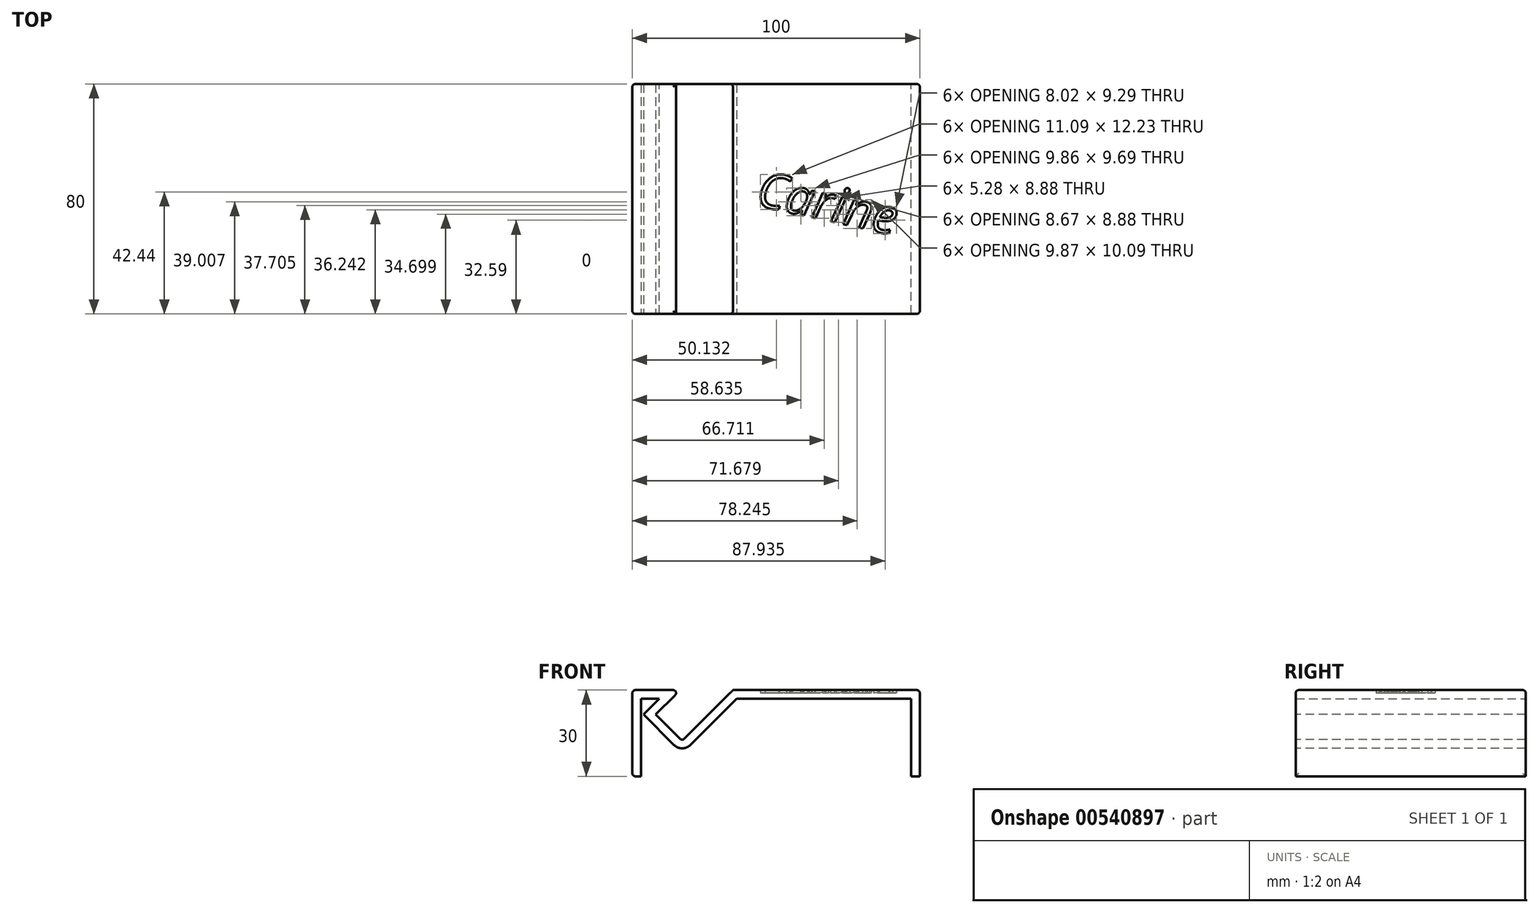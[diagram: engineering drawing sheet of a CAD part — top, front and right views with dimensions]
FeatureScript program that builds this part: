
annotation { "Feature Type Name" : "Feature", "Feature Type Description" : "" }
export const myFeature = defineFeature(function(context is Context, id is Id, definition is map)
    precondition{}
    {
        {
            var Q0;
            Q0=qCreatedBy(makeId("Top.planeOp"),FACE);
            var sketch = newSketch(context, id + "F0", { "sketchPlane" : qUnion([Q0])});
            skLineSegment(sketch, "E0.bottom", {"start": v(-50, -40) * mm, "end": v(50, -40) * mm});
            skLineSegment(sketch, "E0.top", {"start": v(-50, 40) * mm, "end": v(50, 40) * mm});
            skLineSegment(sketch, "E0.left", {"start": v(-50, -40) * mm, "end": v(-50, 40) * mm});
            skLineSegment(sketch, "E0.right", {"start": v(50, -40) * mm, "end": v(50, 40) * mm});
            skPoint(sketch, "E0.middle", {"position": v(0, 0) * mm});
            skSolve(sketch);
        }
        {
            var Q0;
            Q0=makeQuery(id+"F0.imprint","IMPRINT",FACE,{"disambiguationData":[TD([[makeQuery(id+"F0.imprint","IMPRINT",EDGE,{"derivedFrom":sQuery(id+"F0.wireOp",EDGE,"E0.bottom")}),1.0]])]});
            extrude(context, id + "F1", {"entities" : qUnion([Q0]), "depth" : 30 * mm, "offsetDistance" : 25 * mm});
        }
        {
            var Q0;
            Q0=makeQuery(id+"F1.opExtrude","SWEPT_FACE",FACE,{"disambiguationData":[OSD([sQuery(id+"F0.wireOp",EDGE,"E0.bottom")])]});
            var sketch = newSketch(context, id + "F2", { "sketchPlane" : qUnion([Q0])});
            skLineSegment(sketch, "E1.bottom", {"start": v(-32.68, 12.32) * mm, "end": v(-15, 30) * mm});
            skLineSegment(sketch, "E1.top", {"start": v(-41.87, 21.51) * mm, "end": v(-24.2, 39.2) * mm});
            skLineSegment(sketch, "E1.left", {"start": v(-32.68, 12.32) * mm, "end": v(-41.87, 21.51) * mm});
            skLineSegment(sketch, "E1.right", {"start": v(-15, 30) * mm, "end": v(-24.2, 39.2) * mm});
            skSolve(sketch);
        }
        {
            var Q0;
            Q0 = qSketchRegion(id + "F2", true);
            extrude(context, id + "F3", {"entities" : qUnion([Q0]), "operationType" : NewBodyOperationType.REMOVE, "oppositeDirection" : true, "depth" : 80 * mm, "offsetDistance" : 25 * mm});
        }
        {
            var Q0;
            Q0=makeQuery(id+"F3.boolean.opBoolean","INTERSECT",EDGE,{"derivedFrom":[makeQuery(id+"F1.opExtrude","CAP_FACE",FACE,{"disambiguationData":[OSD([sQuery(id+"F0.wireOp",EDGE,"E0.bottom"),sQuery(id+"F0.wireOp",EDGE,"E0.top"),sQuery(id+"F0.wireOp",EDGE,"E0.left"),sQuery(id+"F0.wireOp",EDGE,"E0.right")])],"isStart":false}),makeQuery(id+"F3.opExtrude","SWEPT_FACE",FACE,{"disambiguationData":[OSD([sQuery(id+"F2.wireOp",EDGE,"E1.top")])]})]});
            var Q1;
            Q1=makeQuery(id+"F3.boolean.opBoolean","COPY",EDGE,{"derivedFrom":makeQuery(id+"F3.opExtrude","SWEPT_EDGE",EDGE,{"disambiguationData":[OSD([sQuery(id+"F0.wireOp",EDGE,"E0.bottom"),sQuery(id+"F2.wireOp",EDGE,"E1.bottom"),sQuery(id+"F2.wireOp",EDGE,"E1.right")])]})});
            var Q2;
            Q2=makeQuery(id+"F3.boolean.opBoolean","COPY",EDGE,{"derivedFrom":makeQuery(id+"F3.opExtrude","CAP_EDGE",EDGE,{"disambiguationData":[OSD([sQuery(id+"F2.wireOp",EDGE,"E1.left")])],"isStart":true})});
            var Q3;
            Q3=makeQuery(id+"F3.boolean.opBoolean","COPY",EDGE,{"derivedFrom":makeQuery(id+"F3.opExtrude","SWEPT_EDGE",EDGE,{"disambiguationData":[OSD([sQuery(id+"F2.wireOp",EDGE,"E1.bottom"),sQuery(id+"F2.wireOp",EDGE,"E1.left")])]})});
            var Q4;
            Q4=makeQuery(id+"F1.opExtrude","CAP_EDGE",EDGE,{"disambiguationData":[OSD([sQuery(id+"F0.wireOp",EDGE,"E0.left")])],"isStart":false});
            var Q5;
            Q5=makeQuery(id+"F1.opExtrude","SWEPT_EDGE",EDGE,{"disambiguationData":[OSD([sQuery(id+"F0.wireOp",EDGE,"E0.top"),sQuery(id+"F0.wireOp",EDGE,"E0.left")])]});
            var Q6;
            Q6=makeQuery(id+"F1.opExtrude","CAP_EDGE",EDGE,{"disambiguationData":[OSD([sQuery(id+"F0.wireOp",EDGE,"E0.left")])],"isStart":true});
            var Q7;
            Q7=makeQuery(id+"F1.opExtrude","SWEPT_EDGE",EDGE,{"disambiguationData":[OSD([sQuery(id+"F0.wireOp",EDGE,"E0.bottom"),sQuery(id+"F0.wireOp",EDGE,"E0.left")])]});
            var Q8;
            {var subQ0=sQuery(id+"F0.wireOp",EDGE,"E0.bottom");var subQ1=sQuery(id+"F0.wireOp",EDGE,"E0.left");Q8=makeQuery(id+"F3.boolean.opBoolean","SPLIT",EDGE,{"disambiguationData":[TD([makeQuery(id+"F1.opExtrude","SWEPT_FACE",FACE,{"disambiguationData":[OSD([subQ1])]})])],"derivedFrom":makeQuery(id+"F1.opExtrude","CAP_EDGE",EDGE,{"disambiguationData":[OSD([subQ0])],"isStart":false})});}
            var Q9;
            Q9=makeQuery(id+"F3.boolean.opBoolean","COPY",EDGE,{"derivedFrom":makeQuery(id+"F3.opExtrude","CAP_EDGE",EDGE,{"disambiguationData":[OSD([sQuery(id+"F2.wireOp",EDGE,"E1.bottom")])],"isStart":true})});
            var Q10;
            {var subQ0=sQuery(id+"F0.wireOp",EDGE,"E0.bottom");var subQ1=sQuery(id+"F0.wireOp",EDGE,"E0.right");Q10=makeQuery(id+"F3.boolean.opBoolean","SPLIT",EDGE,{"disambiguationData":[TD([makeQuery(id+"F1.opExtrude","SWEPT_FACE",FACE,{"disambiguationData":[OSD([subQ1])]})])],"derivedFrom":makeQuery(id+"F1.opExtrude","CAP_EDGE",EDGE,{"disambiguationData":[OSD([subQ0])],"isStart":false})});}
            var Q11;
            Q11=makeQuery(id+"F1.opExtrude","CAP_EDGE",EDGE,{"disambiguationData":[OSD([sQuery(id+"F0.wireOp",EDGE,"E0.right")])],"isStart":false});
            var Q12;
            {var subQ0=sQuery(id+"F0.wireOp",EDGE,"E0.right");var subQ1=sQuery(id+"F0.wireOp",EDGE,"E0.top");Q12=makeQuery(id+"F3.boolean.opBoolean","SPLIT",EDGE,{"disambiguationData":[TD([makeQuery(id+"F1.opExtrude","SWEPT_FACE",FACE,{"disambiguationData":[OSD([subQ0])]})])],"derivedFrom":makeQuery(id+"F1.opExtrude","CAP_EDGE",EDGE,{"disambiguationData":[OSD([subQ1])],"isStart":false})});}
            var Q13;
            Q13=makeQuery(id+"F3.boolean.opBoolean","COPY",EDGE,{"derivedFrom":makeQuery(id+"F3.opExtrude","CAP_EDGE",EDGE,{"disambiguationData":[OSD([sQuery(id+"F2.wireOp",EDGE,"E1.bottom")])],"isStart":false})});
            var Q14;
            Q14=makeQuery(id+"F1.opExtrude","SWEPT_EDGE",EDGE,{"disambiguationData":[OSD([sQuery(id+"F0.wireOp",EDGE,"E0.top"),sQuery(id+"F0.wireOp",EDGE,"E0.right")])]});
            var Q15;
            Q15=makeQuery(id+"F1.opExtrude","SWEPT_EDGE",EDGE,{"disambiguationData":[OSD([sQuery(id+"F0.wireOp",EDGE,"E0.bottom"),sQuery(id+"F0.wireOp",EDGE,"E0.right")])]});
            var Q16;
            {var subQ0=sQuery(id+"F0.wireOp",EDGE,"E0.left");var subQ1=sQuery(id+"F0.wireOp",EDGE,"E0.top");Q16=makeQuery(id+"F3.boolean.opBoolean","SPLIT",EDGE,{"disambiguationData":[TD([makeQuery(id+"F1.opExtrude","SWEPT_FACE",FACE,{"disambiguationData":[OSD([subQ0])]})])],"derivedFrom":makeQuery(id+"F1.opExtrude","CAP_EDGE",EDGE,{"disambiguationData":[OSD([subQ1])],"isStart":false})});}
            fillet(context, id + "F4", {"entities" : qUnion([Q0, Q1, Q2, Q3, Q4, Q5, Q6, Q7, Q8, Q9, Q10, Q11, Q12, Q13, Q14, Q15, Q16]), "radius" : 1 * mm, "tangentPropagation" : true, "allowEdgeOverflow" : false});
        }
        {
            var Q0;
            Q0=makeQuery(id+"F1.opExtrude","CAP_FACE",FACE,{"disambiguationData":[OSD([sQuery(id+"F0.wireOp",EDGE,"E0.bottom"),sQuery(id+"F0.wireOp",EDGE,"E0.top"),sQuery(id+"F0.wireOp",EDGE,"E0.left"),sQuery(id+"F0.wireOp",EDGE,"E0.right")])],"isStart":true});
            var Q1;
            Q1=makeQuery(id+"F1.opExtrude","SWEPT_FACE",FACE,{"disambiguationData":[OSD([sQuery(id+"F0.wireOp",EDGE,"E0.bottom")])]});
            var Q2;
            Q2=makeQuery(id+"F1.opExtrude","SWEPT_FACE",FACE,{"disambiguationData":[OSD([sQuery(id+"F0.wireOp",EDGE,"E0.top")])]});
            shell(context, id + "F5", {"entities" : qUnion([Q0, Q1, Q2]), "thickness" : 3 * mm});
        }
        {
            var Q0;
            {var subQ0=sQuery(id+"F0.wireOp",EDGE,"E0.bottom");var subQ1=sQuery(id+"F0.wireOp",EDGE,"E0.right");var subQ2=sQuery(id+"F0.wireOp",EDGE,"E0.top");Q0=makeQuery(id+"F3.boolean.opBoolean","SPLIT",FACE,{"disambiguationData":[TD([makeQuery(id+"F1.opExtrude","SWEPT_FACE",FACE,{"disambiguationData":[OSD([subQ1])]})])],"derivedFrom":makeQuery(id+"F1.opExtrude","CAP_FACE",FACE,{"disambiguationData":[OSD([subQ0,subQ2,sQuery(id+"F0.wireOp",EDGE,"E0.left"),subQ1])],"isStart":false})});}
            var sketch = newSketch(context, id + "F6", { "sketchPlane" : qUnion([Q0])});
            skText(sketch, "E2", { "text": "Carine\n", "fontName": "OpenSans-Italic.ttf"});
            const initialGuessF6  = {"E2": [-0.00745, -0.00208, 0.97673, -0.21445, 0.0124]};
            skSetInitialGuess(sketch, initialGuessF6);
            skSolve(sketch);
        }
        {
            var Q0;
            Q0 = qSketchRegion(id + "F6", true);
            extrude(context, id + "F7", {"entities" : qUnion([Q0]), "operationType" : NewBodyOperationType.REMOVE, "oppositeDirection" : true, "depth" : 1 * mm, "offsetDistance" : 25 * mm});
        }
    });
